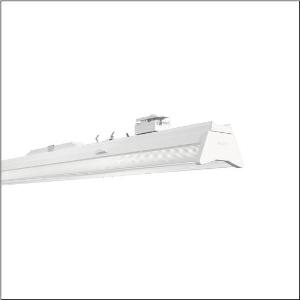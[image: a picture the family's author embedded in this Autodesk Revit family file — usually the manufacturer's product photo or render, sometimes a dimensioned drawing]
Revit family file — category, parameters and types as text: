
# Revit family: licross_11_performance_ho_51td16dn4fxm
name_source: partatom
category: Lighting Fixtures
units: mm (PartAtom-declared; Revit-internal decimal feet)

## family parameters
Cut with Voids When Loaded = No
Host = Face
Light Source = No
Part Type = Normal
Room Calculation Point = No
Round Connector Dimension = Use Diameter
Shared = No

## types (1)
- --- (1 x LED, 15460 lm, 87.3 W, 4000K)
    Apparent Load = 87 VA
    CIE Flux Codes = 63 87 95 78 100
    Color Rendering = 80
    Color Temperature = 4000K
    Default Elevation = 1800 mm
    Description = Licross 11 Performance HO, luminaire insert, of sheet steel, galvanised, coil coated, white, length: 1.500mm, width: 120mm, height: 123mm, LED rated luminous flux: 15.460lm, light colour: 840, SDCM (Standard Deviation of Colour Matching)MacAdam ≤ 2 SDCM (initial), control gear: DALI 2, with plug, 5-pole, with phase selection, mains connection: 220..240V, AC, 50/60Hz, rated input power: 87W, internal wiring halogen-free, primary light control with lens, of plastic, primary optical cover: cover, of PMMA, light emission: direct/indirect distribution, primary light characteristic: symmetric, protection rating (complete): IP54, insulation class (complete): insulation class I (protective earthing), certification: CE, ENEC, VDE, UKCA, protection symbol: D if used in an environment with non-conductive dust loads with corresponding accessories, impact resistance: IK06, permissible ambient temperature for indoor applications: -25..+30°C, corresponds to IFS (International Featured Standards) requirements for safety and quality in the food industry, reducing of maximum allowable ambient temperature of 5°C with ceiling mounting, LABS conformity tested according to VDMA 24364:2018-05, The light source and the operating device comply with the requirements of the Ecodesign Regulation (EU) 2019/2020 and are replaceable in accordance with this regulation, packaging unit: 1 piece
    Height = 114 mm
    Lamp = 1 x LED
    Lamp Light Flux = 15460 lm
    Lamp Power = 87.3 W
    Lamp count = 1
    Length = 1500 mm
    Luminous efficacy = 177 lm/W
    Manufacturer = Siteco
    ModVariant = No
    Model = 51TD16DN4FXM
    Mounting Place = Ceiling
    Mounting Type = Pendant
    Number of Poles = 1
    OnlyDefault = Yes
    Power Factor = 1
    Product Name = Licross 11 Performance HO
    Product group = luminaire insert | ceiling pendant
    ProductGroupID = 901
    Protection Class = Protection class I
    Protection Degree = IP 54
    RLX_Detail_Level = 1
    RLX_Emergency_Light_Flux = 0 lm
    RLX_Emergency_Type = 0
    RLX_Emergency_Type_DB = No
    RlxData = <blob elided: 34461 chars, md5=4ea3b2c0>
    Socket = socket
    Standby Power = 0 W
    System Light Flux = 15460 lm
    System Power = 87 W
    Type Comments = factory setting: luminous flux: 100 % | dim-lin: 254 | 589 mA
    Type Image = l_1256138.jpg
    URL = http://relux.com
    VarID = @adj_104491
    Voltage = 0 V
    Weight = 0.00 kg
    Width = 120 mm

## geometry (parser evidence)
native form markers: Blend x4, Sweep x15
no freeform markers — native parametric forms only
